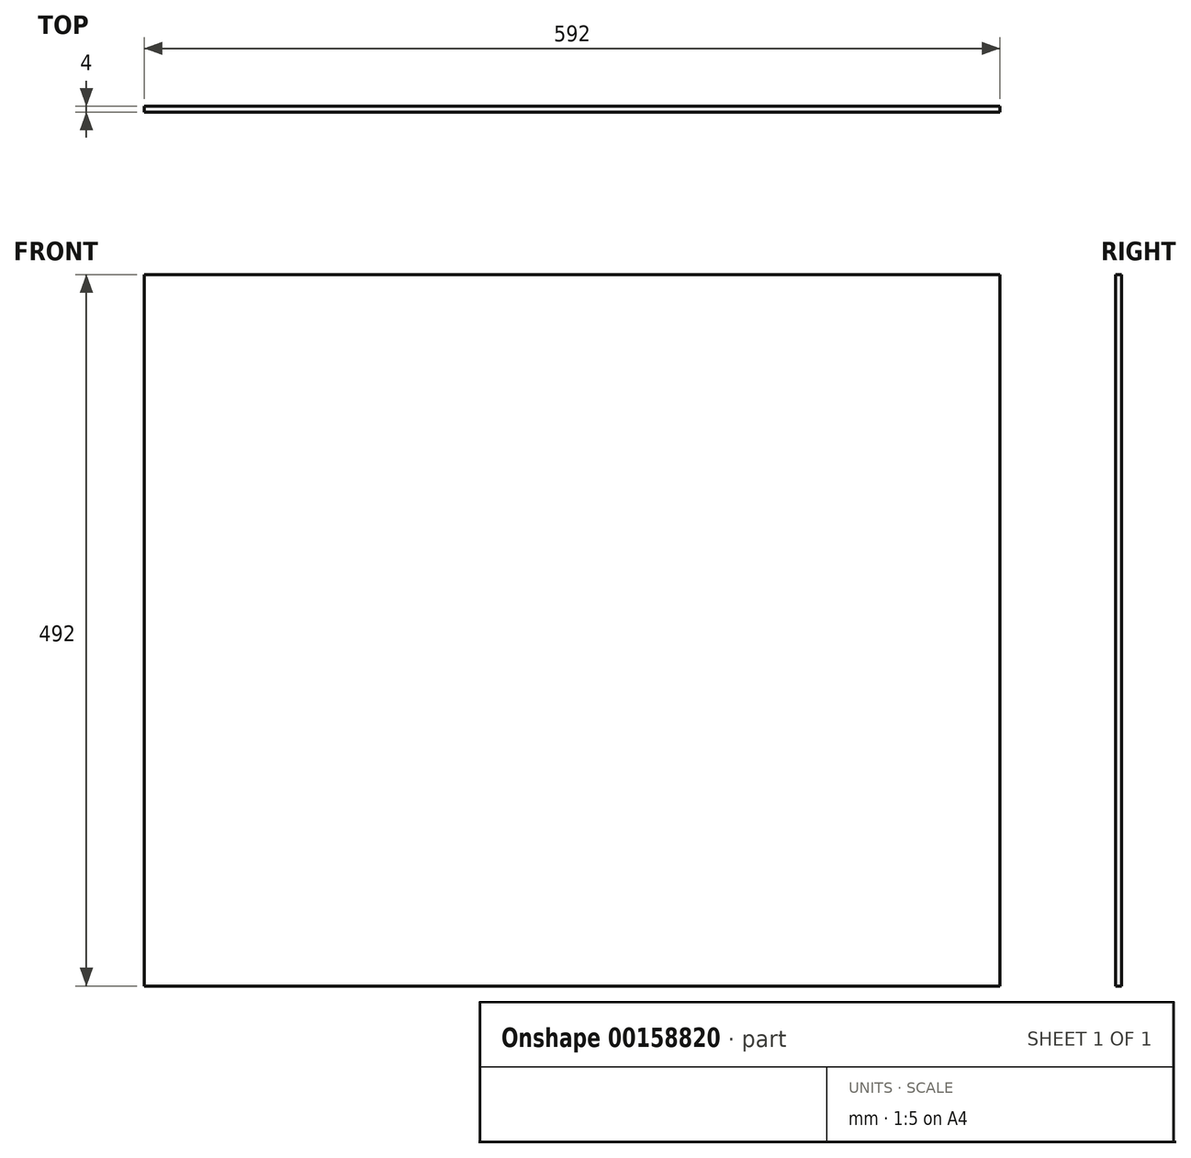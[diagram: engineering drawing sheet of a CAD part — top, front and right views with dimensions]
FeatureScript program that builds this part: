
annotation { "Feature Type Name" : "Feature", "Feature Type Description" : "" }
export const myFeature = defineFeature(function(context is Context, id is Id, definition is map)
    precondition{}
    {
        {
            var Q0;
            Q0=qCreatedBy(makeId("Front.planeOp"),FACE);
            var sketch = newSketch(context, id + "F0", { "sketchPlane" : qUnion([Q0])});
            skLineSegment(sketch, "E0.bottom", {"start": v(0, 0) * mm, "end": v(592, 0) * mm});
            skLineSegment(sketch, "E0.top", {"start": v(0, 492) * mm, "end": v(592, 492) * mm});
            skLineSegment(sketch, "E0.left", {"start": v(0, 0) * mm, "end": v(0, 492) * mm});
            skLineSegment(sketch, "E0.right", {"start": v(592, 0) * mm, "end": v(592, 492) * mm});
            skSolve(sketch);
        }
        {
            var Q0;
            Q0 = qSketchRegion(id + "F0", true);
            extrude(context, id + "F1", {"entities" : qUnion([Q0]), "depth" : 4 * mm});
        }
    });
